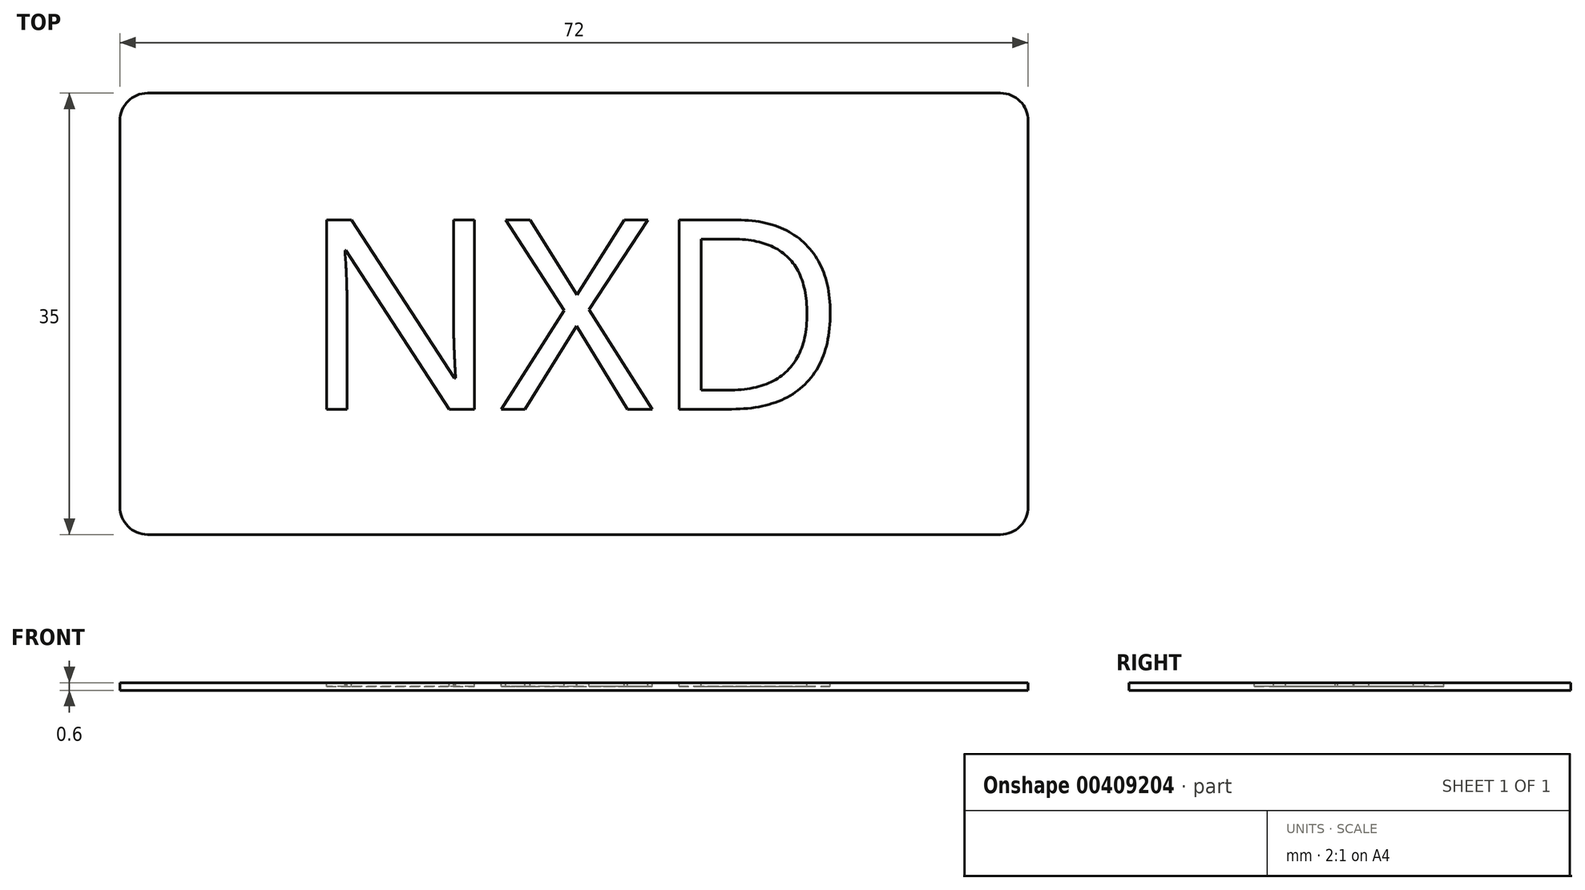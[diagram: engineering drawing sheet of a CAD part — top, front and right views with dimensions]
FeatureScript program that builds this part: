
annotation { "Feature Type Name" : "Feature", "Feature Type Description" : "" }
export const myFeature = defineFeature(function(context is Context, id is Id, definition is map)
    precondition{}
    {
        {
            var Q0;
            Q0=qCreatedBy(makeId("Top.planeOp"),FACE);
            var sketch = newSketch(context, id + "F0", { "sketchPlane" : qUnion([Q0])});
            skLineSegment(sketch, "E0.bottom", {"start": v(36, -17.5) * mm, "end": v(-36, -17.5) * mm});
            skLineSegment(sketch, "E0.top", {"start": v(36, 17.5) * mm, "end": v(-36, 17.5) * mm});
            skLineSegment(sketch, "E0.left", {"start": v(36, -17.5) * mm, "end": v(36, 17.5) * mm});
            skLineSegment(sketch, "E0.right", {"start": v(-36, -17.5) * mm, "end": v(-36, 17.5) * mm});
            skPoint(sketch, "E0.middle", {"position": v(0, 0) * mm});
            skSolve(sketch);
        }
        {
            var Q0;
            Q0 = qSketchRegion(id + "F0", true);
            extrude(context, id + "F1", {"entities" : qUnion([Q0]), "depth" : 0.6 * mm});
        }
        {
            var Q0;
            Q0=makeQuery(id+"F1.opExtrude","CAP_FACE",FACE,{"disambiguationData":[OSD([sQuery(id+"F0.wireOp",EDGE,"E0.bottom"),sQuery(id+"F0.wireOp",EDGE,"E0.top"),sQuery(id+"F0.wireOp",EDGE,"E0.left"),sQuery(id+"F0.wireOp",EDGE,"E0.right")])],"isStart":false});
            var sketch = newSketch(context, id + "F2", { "sketchPlane" : qUnion([Q0])});
            skText(sketch, "E1", { "text": "NXD", "fontName": "OpenSans-Regular.ttf"});
            const initialGuessF2  = {"E1": [-0.02167, -0.00756, 1, 0, 0.01512]};
            skSetInitialGuess(sketch, initialGuessF2);
            skSolve(sketch);
        }
        {
            var Q0;
            Q0=makeQuery(id+"F2.imprint","IMPRINT",FACE,{"disambiguationData":[TD([[makeQuery(id+"F2.imprint","IMPRINT",EDGE,{"derivedFrom":sQuery(id+"F2.wireOp",EDGE,"E1.sketch_text.stroke-0")}),-1.0]])]});
            var Q1;
            Q1 = qSketchRegion(id + "F2", true);
            extrude(context, id + "F3", {"entities" : qUnion([Q0, Q1]), "operationType" : NewBodyOperationType.REMOVE, "oppositeDirection" : true, "depth" : 0.3 * mm});
        }
        {
            var Q0;
            Q0=makeQuery(id+"F1.opExtrude","SWEPT_EDGE",EDGE,{"disambiguationData":[OSD([sQuery(id+"F0.wireOp",EDGE,"E0.bottom"),sQuery(id+"F0.wireOp",EDGE,"E0.right")])]});
            var Q1;
            Q1=makeQuery(id+"F1.opExtrude","SWEPT_EDGE",EDGE,{"disambiguationData":[OSD([sQuery(id+"F0.wireOp",EDGE,"E0.bottom"),sQuery(id+"F0.wireOp",EDGE,"E0.left")])]});
            var Q2;
            Q2=makeQuery(id+"F1.opExtrude","SWEPT_EDGE",EDGE,{"disambiguationData":[OSD([sQuery(id+"F0.wireOp",EDGE,"E0.top"),sQuery(id+"F0.wireOp",EDGE,"E0.left")])]});
            var Q3;
            Q3=makeQuery(id+"F1.opExtrude","SWEPT_EDGE",EDGE,{"disambiguationData":[OSD([sQuery(id+"F0.wireOp",EDGE,"E0.top"),sQuery(id+"F0.wireOp",EDGE,"E0.right")])]});
            fillet(context, id + "F4", {"entities" : qUnion([Q0, Q1, Q2, Q3]), "radius" : 2.2 * mm, "tangentPropagation" : true, "allowEdgeOverflow" : false});
        }
    });
